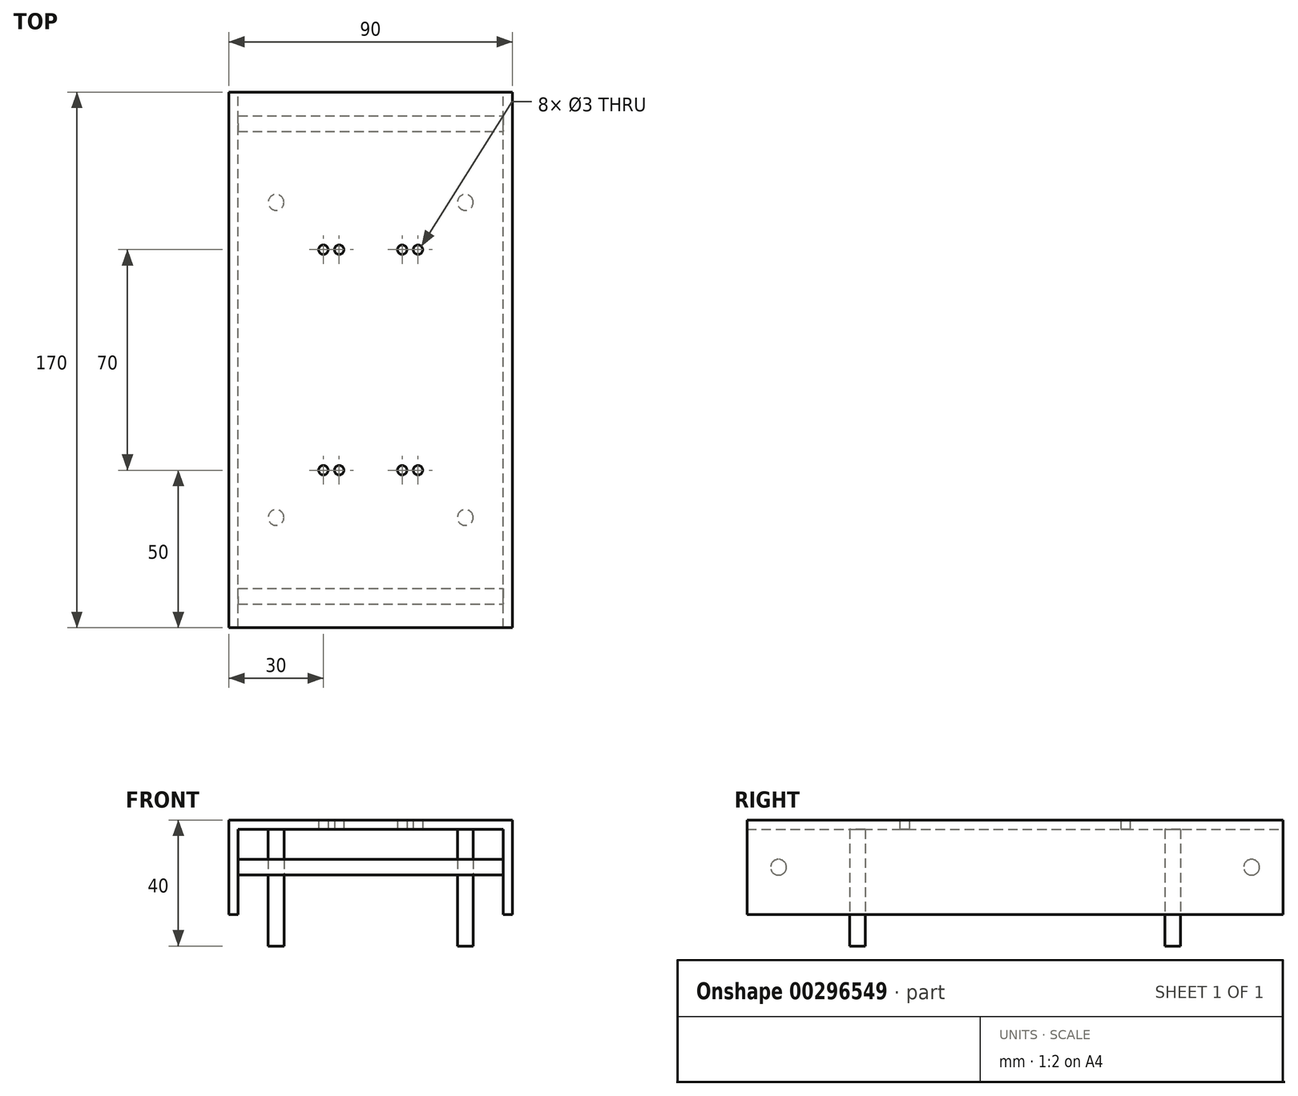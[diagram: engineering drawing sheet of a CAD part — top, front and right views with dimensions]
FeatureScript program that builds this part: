
annotation { "Feature Type Name" : "Feature", "Feature Type Description" : "" }
export const myFeature = defineFeature(function(context is Context, id is Id, definition is map)
    precondition{}
    {
        {
            var Q0;
            Q0=qCreatedBy(makeId("Front.planeOp"),FACE);
            var sketch = newSketch(context, id + "F0", { "sketchPlane" : qUnion([Q0])});
            skLineSegment(sketch, "E0.bottom", {"start": v(45, -15) * mm, "end": v(42, -15) * mm});
            skLineSegment(sketch, "E0.top", {"start": v(45, 15) * mm, "end": v(-45, 15) * mm});
            skLineSegment(sketch, "E0.left", {"start": v(45, -15) * mm, "end": v(45, 15) * mm});
            skLineSegment(sketch, "E0.right", {"start": v(-45, -15) * mm, "end": v(-45, 15) * mm});
            skPoint(sketch, "E0.middle", {"position": v(0, 0) * mm});
            skLineSegment(sketch, "E1", {"start": v(-42, -15) * mm, "end": v(-45, -15) * mm});
            skLineSegment(sketch, "E2", {"start": v(-42, -15) * mm, "end": v(-42, 12) * mm});
            skLineSegment(sketch, "E3", {"start": v(-42, 12) * mm, "end": v(42, 12) * mm});
            skLineSegment(sketch, "E4", {"start": v(42, 12) * mm, "end": v(42, -15) * mm});
            skSolve(sketch);
        }
        {
            var Q0;
            Q0 = qSketchRegion(id + "F0", true);
            extrude(context, id + "F1", {"entities" : qUnion([Q0]), "depth" : 170 * mm, "symmetric" : true});
        }
        {
            var Q0;
            Q0=qCreatedBy(makeId("Right.planeOp"),FACE);
            var sketch = newSketch(context, id + "F2", { "sketchPlane" : qUnion([Q0])});
            skCircle(sketch, "E5", {"center": v(-75, 0) * mm, "radius": 2.5 * mm});
            skCircle(sketch, "E6.MirrorC", {"center": v(75, 0) * mm, "radius": 2.5 * mm});
            skSolve(sketch);
        }
        {
            var Q0;
            Q0 = qSketchRegion(id + "F2", true);
            extrude(context, id + "F3", {"entities" : qUnion([Q0]), "operationType" : NewBodyOperationType.ADD, "oppositeDirection" : true, "depth" : 90 * mm, "symmetric" : true});
        }
        {
            var Q0;
            Q0=qCreatedBy(makeId("Top.planeOp"),FACE);
            var sketch = newSketch(context, id + "F4", { "sketchPlane" : qUnion([Q0])});
            skCircle(sketch, "E7", {"center": v(-30, -50) * mm, "radius": 2.5 * mm});
            skCircle(sketch, "E8.MirrorC", {"center": v(30, -50) * mm, "radius": 2.5 * mm});
            skCircle(sketch, "E9.MirrorC", {"center": v(30, 50) * mm, "radius": 2.5 * mm});
            skCircle(sketch, "E10.MirrorC", {"center": v(-30, 50) * mm, "radius": 2.5 * mm});
            skSolve(sketch);
        }
        {
            var Q0;
            Q0 = qSketchRegion(id + "F4", true);
            extrude(context, id + "F5", {"entities" : qUnion([Q0]), "operationType" : NewBodyOperationType.ADD, "depth" : 15 * mm, "hasSecondDirection" : true, "secondDirectionOppositeDirection" : true, "secondDirectionDepth" : 25 * mm});
        }
        {
            var Q0;
            Q0=qCreatedBy(makeId("Top.planeOp"),FACE);
            var sketch = newSketch(context, id + "F6", { "sketchPlane" : qUnion([Q0])});
            skCircle(sketch, "E11", {"center": v(-10, 35) * mm, "radius": 1.5 * mm});
            skCircle(sketch, "E12.MirrorC", {"center": v(10, 35) * mm, "radius": 1.5 * mm});
            skCircle(sketch, "E13.MirrorC", {"center": v(10, -35) * mm, "radius": 1.5 * mm});
            skCircle(sketch, "E14.MirrorC", {"center": v(-10, -35) * mm, "radius": 1.5 * mm});
            skCircle(sketch, "E15.MirrorC", {"center": v(-15, 35) * mm, "radius": 1.5 * mm});
            skCircle(sketch, "E16.MirrorC", {"center": v(15, 35) * mm, "radius": 1.5 * mm});
            skCircle(sketch, "E17.MirrorC", {"center": v(15, -35) * mm, "radius": 1.5 * mm});
            skCircle(sketch, "E18.MirrorC", {"center": v(-15, -35) * mm, "radius": 1.5 * mm});
            skSolve(sketch);
        }
        {
            var Q0;
            Q0 = qSketchRegion(id + "F6", true);
            extrude(context, id + "F7", {"entities" : qUnion([Q0]), "operationType" : NewBodyOperationType.REMOVE, "depth" : 15 * mm});
        }
    });
